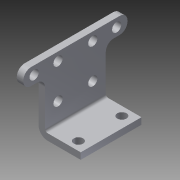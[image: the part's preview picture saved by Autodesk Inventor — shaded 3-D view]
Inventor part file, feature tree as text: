
AUTODESK INVENTOR PART (.ipt)
format: ipt  version: 2013 (Build 170138000, 138)  size: 186,368 bytes
history: native  units: in
note: dims shown in document units (in); Inventor stores cm internally (conversion verified against a paired STEP export)
features: sheet_metal_op x6, other x5, sketch x4, chamfer x1
ambient origin geometry x8: Origin, YZ Plane, XZ Plane, XY Plane, X Axis, Y Axis, Z Axis, Center Point
bodies: Solid1 (feature_tree)
feature tree (16):
  sheet_metal_op  "Face1"
  sheet_metal_op  "Flange1"
  sketch  "Sketch3"  dims[d3=0.266in]
  sheet_metal_op  "Face2"
  chamfer  "Corner Round1"
  sketch  "Sketch1"  dims[d0=1.4in]
  other  "Plate1"
  sketch  "Sketch2"  dims[d2=1.75in]
  other  "Plate2"
  sheet_metal_op  "Bend1"
  sheet_metal_op  "Corner1"
  other  "Plate3"
  sheet_metal_op  "Bend2"
  sketch  "Sketch4"  dims[d4=1.25in d5=0.1875in d6=0.1875in d7=0.0938in d8=0.375in d9=0.1875in d10=2.0in d11=90.0deg d12=0.075in d13=0.75in d14=0.1875in d15=0.1875in d16=0.5in d18=0.266in d19=1.5in d20=1.0in d23=1.0in d24=0.266in d25=1.0in d26=0.625in d27=0.625in d28=0.475in d29=0.475in d30=0.1875in d31=0.1875in d32=0.0938in d33=0.375in d34=0.1875in d35=0.266in d36=0.1875in d37=0.0in d38=0.225in d39=0.185in d40=0.1875in d41=0.0in d42=0.2375in]
  other  "Cut2"
  other  "Cut3"
